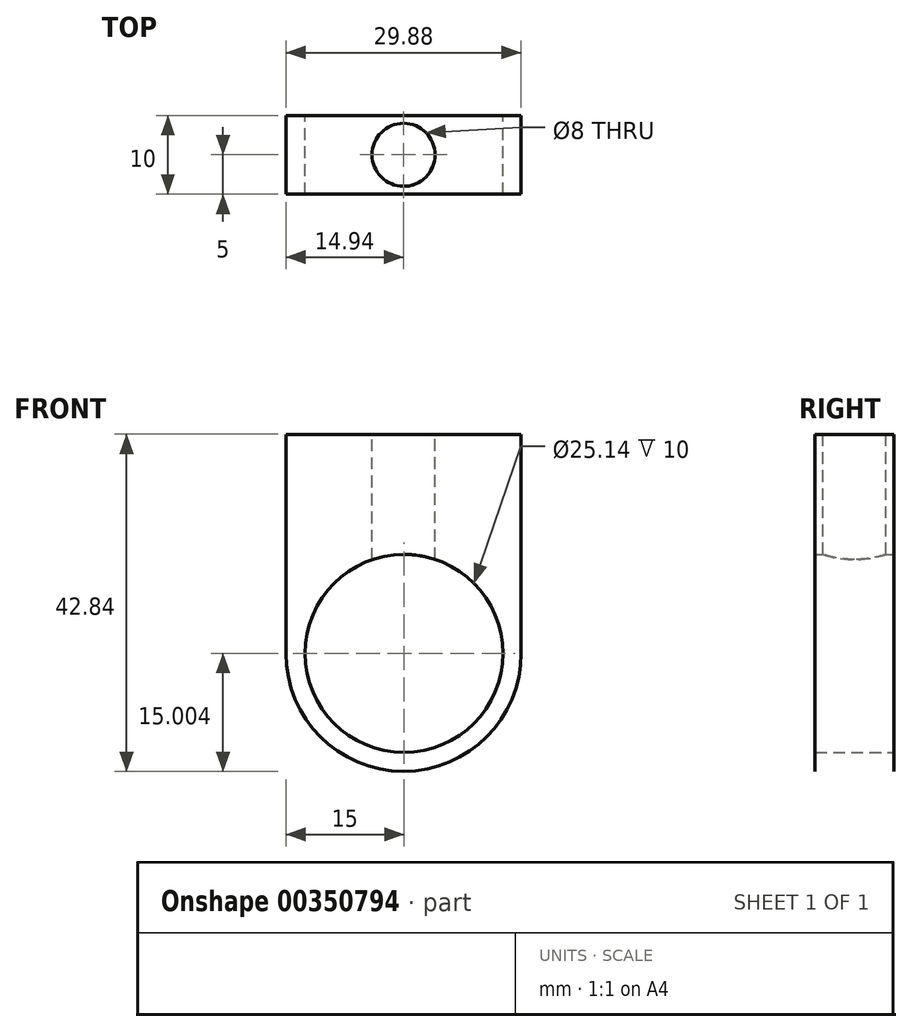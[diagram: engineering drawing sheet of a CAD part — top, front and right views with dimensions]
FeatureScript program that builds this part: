
annotation { "Feature Type Name" : "Feature", "Feature Type Description" : "" }
export const myFeature = defineFeature(function(context is Context, id is Id, definition is map)
    precondition{}
    {
        {
            var Q0;
            Q0=qCreatedBy(makeId("Front.planeOp"),FACE);
            var sketch = newSketch(context, id + "F0", { "sketchPlane" : qUnion([Q0])});
            skLineSegment(sketch, "E0.bottom", {"start": v(9.3, 9.2) * mm, "end": v(-20.58, 9.2) * mm});
            skLineSegment(sketch, "E0.top", {"start": v(-5.58, -33.64) * mm, "end": v(-5.7, -33.64) * mm});
            skLineSegment(sketch, "E0.left", {"start": v(9.3, 9.2) * mm, "end": v(9.3, -18.64) * mm});
            skLineSegment(sketch, "E0.right", {"start": v(-20.58, 9.2) * mm, "end": v(-20.58, -18.64) * mm});
            skPoint(sketch, "E1.visualSharp", {"position": v(9.3, -33.64) * mm});
            skArc(sketch, "E1.filletArc", {"start": v(-5.7, -33.64) * mm, "mid": v(4.9, -29.24) * mm, "end": v(9.3, -18.64) * mm});
            skPoint(sketch, "E2.visualSharp", {"position": v(-20.58, -33.64) * mm});
            skArc(sketch, "E2.filletArc", {"start": v(-20.58, -18.64) * mm, "mid": v(-16.19, -29.24) * mm, "end": v(-5.58, -33.64) * mm});
            skCircle(sketch, "E3", {"center": v(-5.58, -18.64) * mm, "radius": 12.57 * mm});
            skSolve(sketch);
        }
        {
            var Q0;
            Q0=makeQuery(id+"F0.imprint","IMPRINT",FACE,{"disambiguationData":[TD([[makeQuery(id+"F0.imprint","IMPRINT",EDGE,{"derivedFrom":sQuery(id+"F0.wireOp",EDGE,"E0.bottom")}),1.0]])]});
            extrude(context, id + "F1", {"entities" : qUnion([Q0]), "depth" : 10 * mm});
        }
        {
            var Q0;
            Q0=makeQuery(id+"F1.opExtrude","SWEPT_FACE",FACE,{"disambiguationData":[OSD([sQuery(id+"F0.wireOp",EDGE,"E0.bottom")])]});
            var sketch = newSketch(context, id + "F2", { "sketchPlane" : qUnion([Q0])});
            skLineSegment(sketch, "E4", {"start": v(-20.58, 0) * mm, "end": v(-5.64, 0) * mm});
            skCircle(sketch, "E5", {"center": v(-5.64, -5) * mm, "radius": 4 * mm});
            skSolve(sketch);
        }
        {
            var Q0;
            Q0=qSketchRegion(id+"F2",true);
            extrude(context, id + "F3", {"entities" : qUnion([Q0]), "operationType" : NewBodyOperationType.REMOVE, "oppositeDirection" : true, "depth" : 25 * mm});
        }
    });
